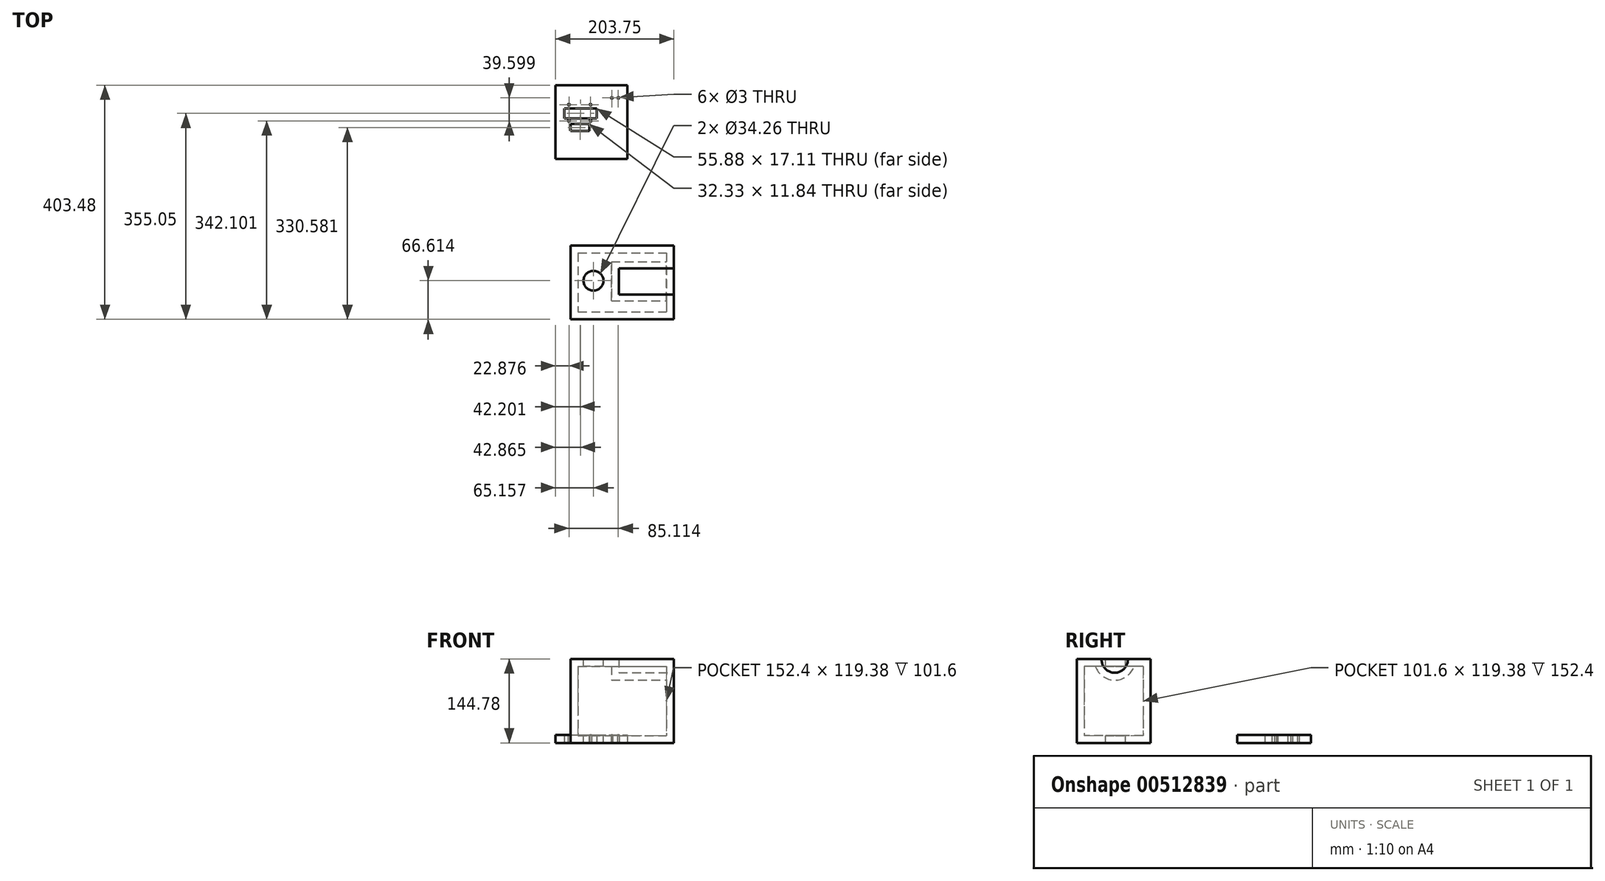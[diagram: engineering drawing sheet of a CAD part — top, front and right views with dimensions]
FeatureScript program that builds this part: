
annotation { "Feature Type Name" : "Feature", "Feature Type Description" : "" }
export const myFeature = defineFeature(function(context is Context, id is Id, definition is map)
    precondition{}
    {
        {
            var Q0;
            Q0=qCreatedBy(makeId("Top.planeOp"),FACE);
            var sketch = newSketch(context, id + "F0", { "sketchPlane" : qUnion([Q0])});
            skLineSegment(sketch, "E0.bottom", {"start": v(-84.57, 0) * mm, "end": v(38.97, 0) * mm});
            skLineSegment(sketch, "E0.top", {"start": v(-84.57, 127) * mm, "end": v(38.97, 127) * mm});
            skLineSegment(sketch, "E0.left", {"start": v(-84.57, 0) * mm, "end": v(-84.57, 127) * mm});
            skLineSegment(sketch, "E0.right", {"start": v(38.97, 0) * mm, "end": v(38.97, 127) * mm});
            skCircle(sketch, "E1", {"center": v(-61.7, 93.56) * mm, "radius": 1.5 * mm});
            skCircle(sketch, "E2", {"center": v(-61.7, 65.62) * mm, "radius": 1.5 * mm});
            skCircle(sketch, "E3", {"center": v(-24.34, 65.62) * mm, "radius": 1.5 * mm});
            skCircle(sketch, "E4", {"center": v(-24.34, 93.56) * mm, "radius": 1.5 * mm});
            skLineSegment(sketch, "E5.bottom", {"start": v(-69.65, 87.12) * mm, "end": v(-13.77, 87.12) * mm});
            skLineSegment(sketch, "E5.top", {"start": v(-69.65, 70.02) * mm, "end": v(-13.77, 70.02) * mm});
            skLineSegment(sketch, "E5.left", {"start": v(-69.65, 87.12) * mm, "end": v(-69.65, 70.02) * mm});
            skLineSegment(sketch, "E5.right", {"start": v(-13.77, 87.12) * mm, "end": v(-13.77, 70.02) * mm});
            skCircle(sketch, "E6", {"center": v(12.2, 105.22) * mm, "radius": 1.5 * mm});
            skCircle(sketch, "E7", {"center": v(23.42, 105.22) * mm, "radius": 1.5 * mm});
            skSolve(sketch);
        }
        {
            var Q0;
            Q0=makeQuery(id+"F0.imprint","IMPRINT",FACE,{"disambiguationData":[TD([[makeQuery(id+"F0.imprint","IMPRINT",EDGE,{"derivedFrom":sQuery(id+"F0.wireOp",EDGE,"E0.bottom")}),1.0]])]});
            extrude(context, id + "F1", {"entities" : qUnion([Q0]), "depth" : 13.97 * mm});
        }
        {
            var Q0;
            Q0=qCreatedBy(makeId("Top.planeOp"),FACE);
            var sketch = newSketch(context, id + "F2", { "sketchPlane" : qUnion([Q0])});
            skLineSegment(sketch, "E8.bottom", {"start": v(-58.62, -149.48) * mm, "end": v(119.18, -149.48) * mm});
            skLineSegment(sketch, "E8.top", {"start": v(-58.62, -276.48) * mm, "end": v(119.18, -276.48) * mm});
            skLineSegment(sketch, "E8.left", {"start": v(-58.62, -149.48) * mm, "end": v(-58.62, -276.48) * mm});
            skLineSegment(sketch, "E8.right", {"start": v(119.18, -149.48) * mm, "end": v(119.18, -276.48) * mm});
            skSolve(sketch);
        }
        {
            var Q0;
            Q0=makeQuery(id+"F2.imprint","IMPRINT",FACE,{"disambiguationData":[TD([[makeQuery(id+"F2.imprint","IMPRINT",EDGE,{"derivedFrom":sQuery(id+"F2.wireOp",EDGE,"E8.bottom")}),-1.0]])]});
            extrude(context, id + "F3", {"entities" : qUnion([Q0]), "depth" : 144.78 * mm});
        }
        {
            var Q0;
            Q0=makeQuery(id+"F3.opExtrude","CAP_FACE",FACE,{"disambiguationData":[OSD([sQuery(id+"F2.wireOp",EDGE,"E8.bottom"),sQuery(id+"F2.wireOp",EDGE,"E8.top"),sQuery(id+"F2.wireOp",EDGE,"E8.left"),sQuery(id+"F2.wireOp",EDGE,"E8.right")])],"isStart":false});
            var sketch = newSketch(context, id + "F4", { "sketchPlane" : qUnion([Q0])});
            skLineSegment(sketch, "E9.bottom", {"start": v(119.18, -231.17) * mm, "end": v(27.03, -231.17) * mm});
            skLineSegment(sketch, "E10", {"start": v(25.36, -231.17) * mm, "end": v(25.36, -185.58) * mm});
            skLineSegment(sketch, "E11", {"start": v(25.36, -185.58) * mm, "end": v(119.18, -185.58) * mm});
            skSolve(sketch);
        }
        {
            var Q0;
            Q0=makeQuery(id+"F3.opExtrude","SWEPT_FACE",FACE,{"disambiguationData":[OSD([sQuery(id+"F2.wireOp",EDGE,"E8.right")])]});
            var sketch = newSketch(context, id + "F5", { "sketchPlane" : qUnion([Q0])});
            skArc(sketch, "E12", {"start": v(-233.6, 144.78) * mm, "mid": v(-210.99, 120.78) * mm, "end": v(-188.37, 144.78) * mm});
            skSolve(sketch);
        }
        {
            var Q0;
            {var subQ0=sQuery(id+"F5.wireOp",EDGE,"E12");Q0=makeQuery(id+"F5.imprint","IMPRINT",FACE,{"disambiguationData":[TD([[makeQuery(id+"F5.imprint","IMPRINT",EDGE,{"derivedFrom":subQ0}),1.0]])]});}
            extrude(context, id + "F6", {"entities" : qUnion([Q0]), "operationType" : NewBodyOperationType.REMOVE, "oppositeDirection" : true, "depth" : 95 * mm});
        }
        {
            var Q0;
            Q0=makeQuery(id+"F3.opExtrude","SWEPT_FACE",FACE,{"disambiguationData":[OSD([sQuery(id+"F2.wireOp",EDGE,"E8.right")])]});
            var Q1;
            Q1=makeQuery(id+"F3.opExtrude","SWEPT_FACE",FACE,{"disambiguationData":[OSD([sQuery(id+"F2.wireOp",EDGE,"E8.top")])]});
            var Q2;
            Q2=makeQuery(id+"F3.opExtrude","SWEPT_FACE",FACE,{"disambiguationData":[OSD([sQuery(id+"F2.wireOp",EDGE,"E8.left")])]});
            var Q3;
            Q3=makeQuery(id+"F3.opExtrude","CAP_FACE",FACE,{"disambiguationData":[OSD([sQuery(id+"F2.wireOp",EDGE,"E8.bottom"),sQuery(id+"F2.wireOp",EDGE,"E8.top"),sQuery(id+"F2.wireOp",EDGE,"E8.left"),sQuery(id+"F2.wireOp",EDGE,"E8.right")])],"isStart":true});
            var Q4;
            Q4=makeQuery(id+"F3.opExtrude","SWEPT_FACE",FACE,{"disambiguationData":[OSD([sQuery(id+"F2.wireOp",EDGE,"E8.bottom")])]});
            var Q5;
            Q5=makeQuery(id+"F3.opExtrude","SWEPT_BODY",BODY,{"disambiguationData":[OSD([sQuery(id+"F2.wireOp",EDGE,"E8.bottom"),sQuery(id+"F2.wireOp",EDGE,"E8.top"),sQuery(id+"F2.wireOp",EDGE,"E8.left"),sQuery(id+"F2.wireOp",EDGE,"E8.right")])]});
            shell(context, id + "F7", {"isHollow" : true, "entities" : qUnion([Q0, Q1, Q2, Q3, Q4]), "parts" : qUnion([Q5]), "thickness" : 12.7 * mm});
        }
        {
            var Q0;
            {var subQ1=makeQuery(id+"F3.opExtrude","CAP_EDGE",EDGE,{"disambiguationData":[OSD([sQuery(id+"F2.wireOp",EDGE,"E8.bottom")])],"isStart":false});Q0=makeQuery(id+"F4.imprint","IMPRINT",FACE,{"disambiguationData":[TD([[makeQuery(id+"F4.imprint","IMPRINT",EDGE,{"derivedFrom":subQ1}),-1.0]])]});}
            var sketch = newSketch(context, id + "F8", { "sketchPlane" : qUnion([Q0])});
            skCircle(sketch, "E13", {"center": v(-19.41, -209.87) * mm, "radius": 17.13 * mm});
            skSolve(sketch);
        }
        {
            var Q0;
            Q0=makeQuery(id+"F8.imprint","IMPRINT",FACE,{"disambiguationData":[TD([[makeQuery(id+"F8.imprint","IMPRINT",EDGE,{"derivedFrom":sQuery(id+"F8.wireOp",EDGE,"E13")}),1.0]])]});
            extrude(context, id + "F9", {"entities" : qUnion([Q0]), "operationType" : NewBodyOperationType.REMOVE, "endBound" : BoundingType.THROUGH_ALL, "oppositeDirection" : true, "depth" : 25.4 * mm});
        }
        {
            var Q0;
            Q0=makeQuery(id+"F1.opExtrude","CAP_FACE",FACE,{"disambiguationData":[OSD([sQuery(id+"F0.wireOp",EDGE,"E0.bottom"),sQuery(id+"F0.wireOp",EDGE,"E0.top"),sQuery(id+"F0.wireOp",EDGE,"E0.left"),sQuery(id+"F0.wireOp",EDGE,"E0.right"),sQuery(id+"F0.wireOp",EDGE,"E1"),sQuery(id+"F0.wireOp",EDGE,"E2"),sQuery(id+"F0.wireOp",EDGE,"E3"),sQuery(id+"F0.wireOp",EDGE,"E4"),sQuery(id+"F0.wireOp",EDGE,"E5.bottom"),sQuery(id+"F0.wireOp",EDGE,"E5.top"),sQuery(id+"F0.wireOp",EDGE,"E5.left"),sQuery(id+"F0.wireOp",EDGE,"E5.right"),sQuery(id+"F0.wireOp",EDGE,"E6"),sQuery(id+"F0.wireOp",EDGE,"E7")])],"isStart":false});
            var sketch = newSketch(context, id + "F10", { "sketchPlane" : qUnion([Q0])});
            skLineSegment(sketch, "E14.bottom", {"start": v(-58.53, 60.02) * mm, "end": v(-26.2, 60.02) * mm});
            skLineSegment(sketch, "E14.top", {"start": v(-58.53, 48.18) * mm, "end": v(-26.2, 48.18) * mm});
            skLineSegment(sketch, "E14.left", {"start": v(-58.53, 60.02) * mm, "end": v(-58.53, 48.18) * mm});
            skLineSegment(sketch, "E14.right", {"start": v(-26.2, 60.02) * mm, "end": v(-26.2, 48.18) * mm});
            skSolve(sketch);
        }
        {
            var Q0;
            Q0=makeQuery(id+"F10.imprint","IMPRINT",FACE,{"disambiguationData":[TD([[makeQuery(id+"F10.imprint","IMPRINT",EDGE,{"derivedFrom":sQuery(id+"F10.wireOp",EDGE,"E14.bottom")}),-1.0]])]});
            extrude(context, id + "F11", {"entities" : qUnion([Q0]), "operationType" : NewBodyOperationType.REMOVE, "endBound" : BoundingType.THROUGH_ALL, "oppositeDirection" : true, "depth" : 25.4 * mm});
        }
    });
